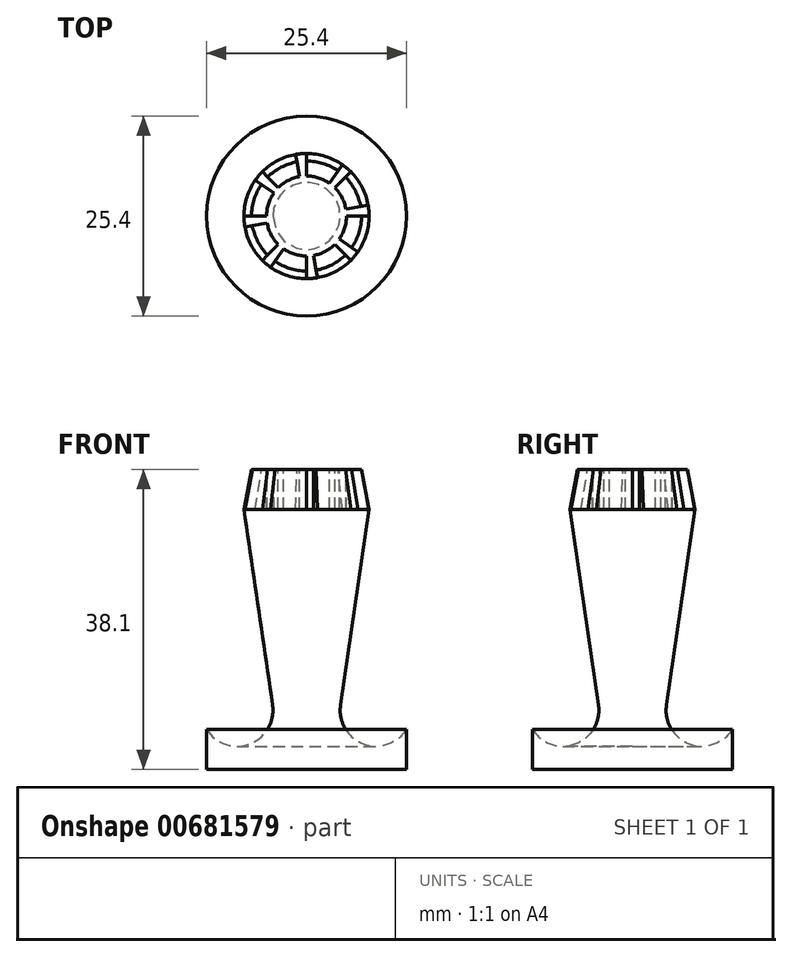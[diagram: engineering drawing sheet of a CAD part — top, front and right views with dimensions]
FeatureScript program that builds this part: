
annotation { "Feature Type Name" : "Feature", "Feature Type Description" : "" }
export const myFeature = defineFeature(function(context is Context, id is Id, definition is map)
    precondition{}
    {
        {
            var Q0;
            Q0=qCreatedBy(makeId("Front.planeOp"),FACE);
            var sketch = newSketch(context, id + "F0", { "sketchPlane" : qUnion([Q0])});
            skLineSegment(sketch, "E0", {"start": v(0, 0) * mm, "end": v(12.7, 0) * mm});
            skLineSegment(sketch, "E1", {"start": v(12.7, 0) * mm, "end": v(12.7, 5.08) * mm});
            skLineSegment(sketch, "E2", {"start": v(0, 0) * mm, "end": v(0, 38.1) * mm});
            skLineSegment(sketch, "E3", {"start": v(0, 38.1) * mm, "end": v(6.99, 38.1) * mm});
            skLineSegment(sketch, "E4", {"start": v(6.99, 38.1) * mm, "end": v(7.95, 33.02) * mm});
            skLineSegment(sketch, "E5", {"start": v(7.95, 33.02) * mm, "end": v(0, 33.02) * mm, "construction": true});
            skArc(sketch, "E6", {"start": v(4.32, 8.17) * mm, "mid": v(7.26, 3.23) * mm, "end": v(12.7, 5.08) * mm});
            skLineSegment(sketch, "E7", {"start": v(7.95, 33.02) * mm, "end": v(4.32, 8.17) * mm});
            skSolve(sketch);
        }
        {
            var Q0;
            Q0=makeQuery(id+"F0.imprint","IMPRINT",FACE,{"disambiguationData":[TD([[makeQuery(id+"F0.imprint","IMPRINT",EDGE,{"derivedFrom":sQuery(id+"F0.wireOp",EDGE,"E0")}),1.0]])]});
            var Q1;
            Q1=sQuery(id+"F0.wireOp",EDGE,"E2");
            revolve(context, id + "F1", {"entities" : qUnion([Q0]), "axis" : qUnion([Q1]), "revolveType" : RevolveType.FULL});
        }
        {
            var Q0;
            Q0=makeQuery(id+"F1.opRevolve","SWEPT_FACE",FACE,{"disambiguationData":[OSD([sQuery(id+"F0.wireOp",EDGE,"E3")])]});
            var sketch = newSketch(context, id + "F2", { "sketchPlane" : qUnion([Q0])});
            skCircle(sketch, "E8", {"center": v(0, 0) * mm, "radius": 5.08 * mm});
            skArc(sketch, "E9.0", {"start": v(1.38, -7.83) * mm, "mid": v(0.7, -7.92) * mm, "end": v(0, -7.95) * mm});
            skLineSegment(sketch, "E10", {"start": v(0.88, -5) * mm, "end": v(1.38, -7.83) * mm});
            skLineSegment(sketch, "E11", {"start": v(0, -5.08) * mm, "end": v(0, -7.95) * mm});
            skLineSegment(sketch, "E12.1.0", {"start": v(4.16, -2.91) * mm, "end": v(6.51, -4.56) * mm});
            skLineSegment(sketch, "E12.1.1", {"start": v(3.6, -3.6) * mm, "end": v(5.62, -5.62) * mm});
            skArc(sketch, "E12.1.2", {"start": v(6.51, -4.56) * mm, "mid": v(6.1, -5.11) * mm, "end": v(5.62, -5.62) * mm});
            skLineSegment(sketch, "E12.2.0", {"start": v(5, 0.88) * mm, "end": v(7.83, 1.38) * mm});
            skLineSegment(sketch, "E12.2.1", {"start": v(5.08, 0) * mm, "end": v(7.95, 0) * mm});
            skArc(sketch, "E12.2.2", {"start": v(7.83, 1.38) * mm, "mid": v(7.92, 0.7) * mm, "end": v(7.95, 0) * mm});
            skLineSegment(sketch, "E12.3.0", {"start": v(2.91, 4.16) * mm, "end": v(4.56, 6.51) * mm});
            skLineSegment(sketch, "E12.3.1", {"start": v(3.6, 3.6) * mm, "end": v(5.62, 5.62) * mm});
            skArc(sketch, "E12.3.2", {"start": v(4.56, 6.51) * mm, "mid": v(5.11, 6.1) * mm, "end": v(5.62, 5.62) * mm});
            skLineSegment(sketch, "E12.4.0", {"start": v(-0.88, 5) * mm, "end": v(-1.38, 7.83) * mm});
            skLineSegment(sketch, "E12.4.1", {"start": v(0, 5.08) * mm, "end": v(0, 7.95) * mm});
            skArc(sketch, "E12.4.2", {"start": v(-1.38, 7.83) * mm, "mid": v(-0.7, 7.92) * mm, "end": v(0, 7.95) * mm});
            skLineSegment(sketch, "E12.5.0", {"start": v(-4.16, 2.91) * mm, "end": v(-6.51, 4.56) * mm});
            skLineSegment(sketch, "E12.5.1", {"start": v(-3.6, 3.6) * mm, "end": v(-5.62, 5.62) * mm});
            skArc(sketch, "E12.5.2", {"start": v(-6.51, 4.56) * mm, "mid": v(-6.1, 5.11) * mm, "end": v(-5.62, 5.62) * mm});
            skLineSegment(sketch, "E12.6.0", {"start": v(-5, -0.88) * mm, "end": v(-7.83, -1.38) * mm});
            skLineSegment(sketch, "E12.6.1", {"start": v(-5.08, 0) * mm, "end": v(-7.95, 0) * mm});
            skArc(sketch, "E12.6.2", {"start": v(-7.83, -1.38) * mm, "mid": v(-7.92, -0.7) * mm, "end": v(-7.95, 0) * mm});
            skLineSegment(sketch, "E12.7.0", {"start": v(-2.91, -4.16) * mm, "end": v(-4.56, -6.51) * mm});
            skLineSegment(sketch, "E12.7.1", {"start": v(-3.6, -3.6) * mm, "end": v(-5.62, -5.62) * mm});
            skArc(sketch, "E12.7.2", {"start": v(-4.56, -6.51) * mm, "mid": v(-5.11, -6.1) * mm, "end": v(-5.62, -5.62) * mm});
            skSolve(sketch);
        }
        {
            var Q0;
            Q0 = qSketchRegion(id + "F2", true);
            extrude(context, id + "F3", {"entities" : qUnion([Q0]), "operationType" : NewBodyOperationType.REMOVE, "oppositeDirection" : true, "depth" : 5.08 * mm, "offsetDistance" : 25.4 * mm});
        }
    });
